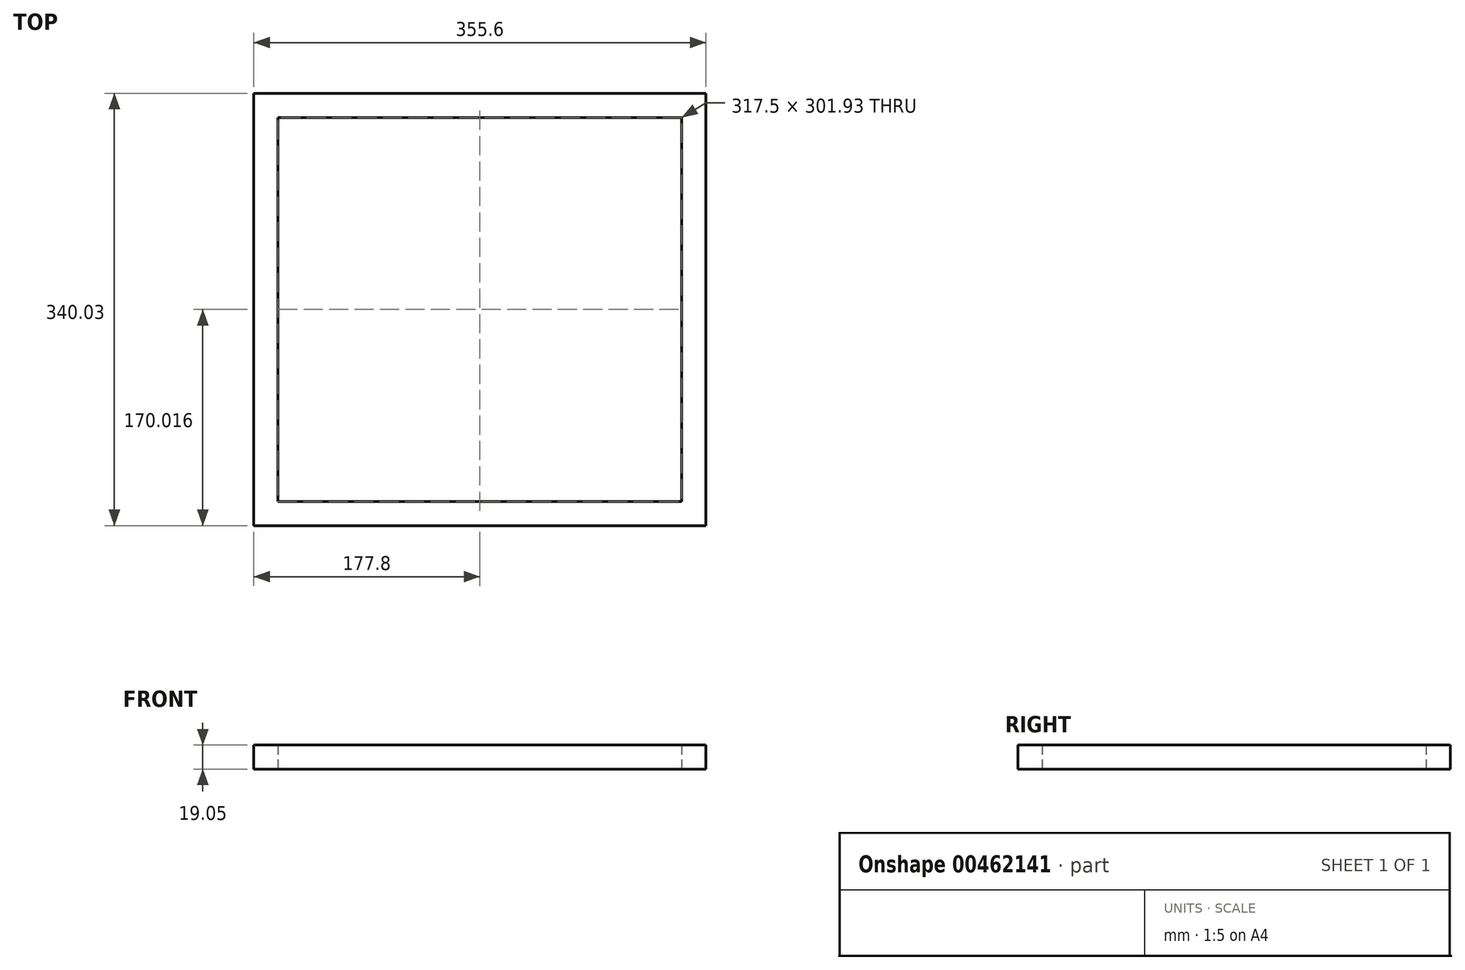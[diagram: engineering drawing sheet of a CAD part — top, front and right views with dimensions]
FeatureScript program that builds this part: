
annotation { "Feature Type Name" : "Feature", "Feature Type Description" : "" }
export const myFeature = defineFeature(function(context is Context, id is Id, definition is map)
    precondition{}
    {
        {
            var Q0;
            Q0=qCreatedBy(makeId("Top.planeOp"),FACE);
            var sketch = newSketch(context, id + "F0", { "sketchPlane" : qUnion([Q0])});
            skLineSegment(sketch, "E0.bottom", {"start": v(0, 0) * mm, "end": v(355.6, 0) * mm});
            skLineSegment(sketch, "E0.top", {"start": v(0, 340.03) * mm, "end": v(355.6, 340.03) * mm});
            skLineSegment(sketch, "E0.left", {"start": v(0, 0) * mm, "end": v(0, 340.03) * mm});
            skLineSegment(sketch, "E0.right", {"start": v(355.6, 0) * mm, "end": v(355.6, 340.03) * mm});
            skLineSegment(sketch, "E1.0", {"start": v(19.05, 320.98) * mm, "end": v(336.55, 320.98) * mm});
            skLineSegment(sketch, "E1.1", {"start": v(19.05, 19.05) * mm, "end": v(19.05, 320.98) * mm});
            skLineSegment(sketch, "E1.2", {"start": v(19.05, 19.05) * mm, "end": v(336.55, 19.05) * mm});
            skLineSegment(sketch, "E1.3", {"start": v(336.55, 19.05) * mm, "end": v(336.55, 320.98) * mm});
            skSolve(sketch);
        }
        {
            var Q0;
            Q0 = qSketchRegion(id + "F0", true);
            extrude(context, id + "F1", {"entities" : qUnion([Q0]), "depth" : 19.05 * mm});
        }
    });
